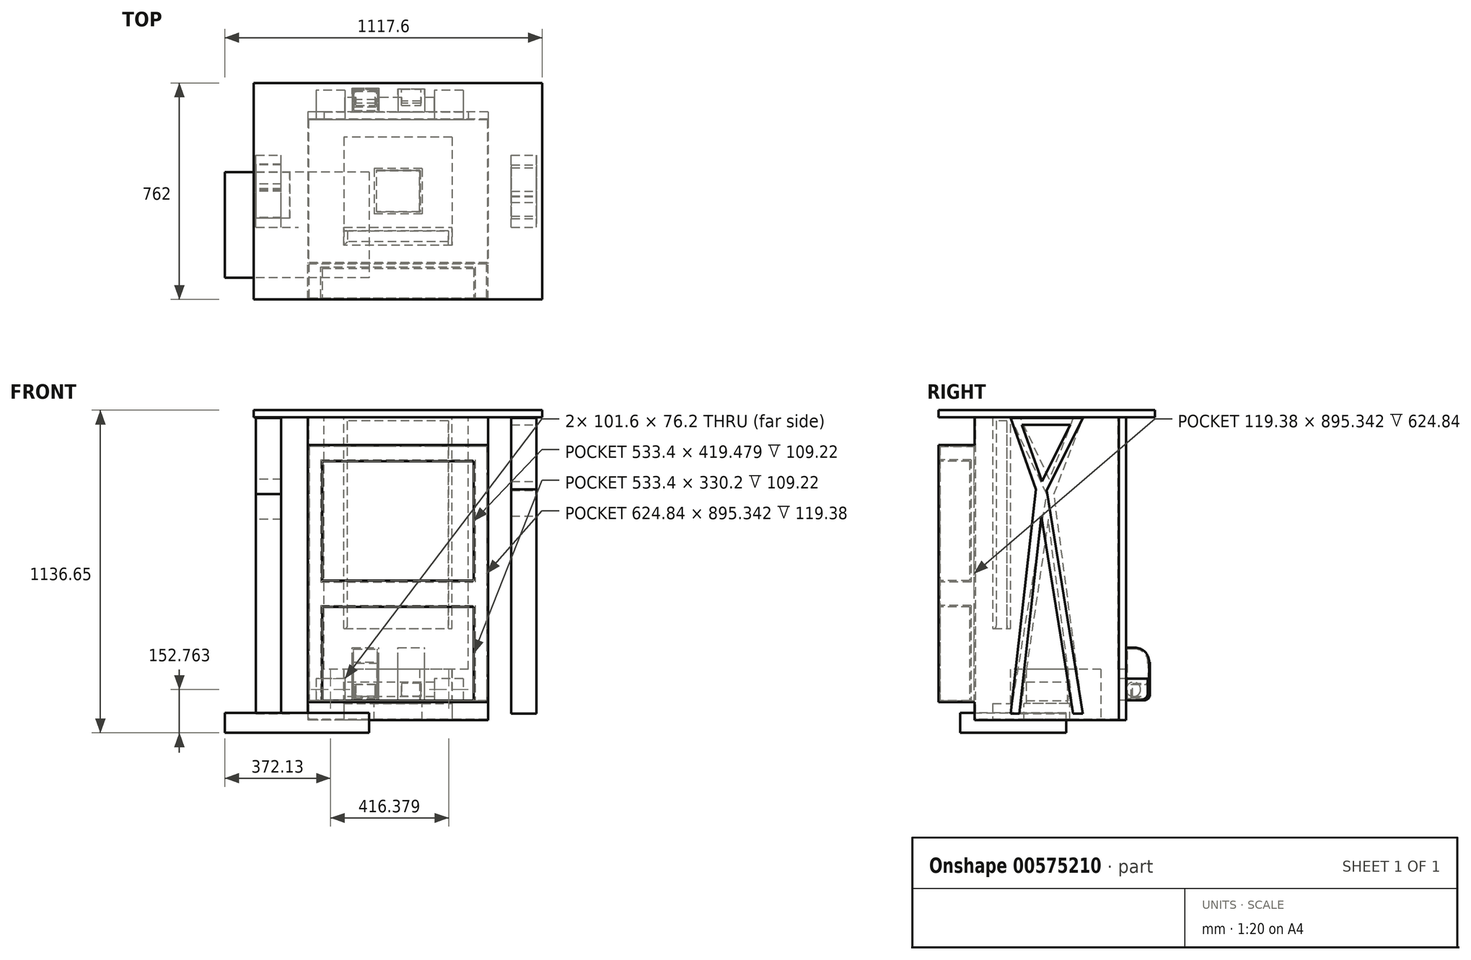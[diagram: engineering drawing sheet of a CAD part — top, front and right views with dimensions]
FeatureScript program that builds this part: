
annotation { "Feature Type Name" : "Feature", "Feature Type Description" : "" }
export const myFeature = defineFeature(function(context is Context, id is Id, definition is map)
    precondition{}
    {
        {
            var Q0;
            Q0=qCreatedBy(makeId("Top.planeOp"),FACE);
            var sketch = newSketch(context, id + "F0", { "sketchPlane" : qUnion([Q0])});
            skLineSegment(sketch, "E0.bottom", {"start": v(609.6, -304.8) * mm, "end": v(-609.6, -304.8) * mm});
            skLineSegment(sketch, "E0.top", {"start": v(609.6, 304.8) * mm, "end": v(-609.6, 304.8) * mm});
            skLineSegment(sketch, "E0.left", {"start": v(609.6, -304.8) * mm, "end": v(609.6, 304.8) * mm});
            skLineSegment(sketch, "E0.right", {"start": v(-609.6, -304.8) * mm, "end": v(-609.6, 304.8) * mm});
            skPoint(sketch, "E0.middle", {"position": v(0, 0) * mm});
            skLineSegment(sketch, "E1.bottom", {"start": v(102.15, -93.34) * mm, "end": v(-102.15, -93.34) * mm});
            skLineSegment(sketch, "E1.top", {"start": v(102.15, 93.34) * mm, "end": v(-102.15, 93.34) * mm});
            skLineSegment(sketch, "E1.left", {"start": v(102.15, -93.34) * mm, "end": v(102.15, 93.34) * mm});
            skLineSegment(sketch, "E1.right", {"start": v(-102.15, -93.34) * mm, "end": v(-102.15, 93.34) * mm});
            skLineSegment(sketch, "E2.bottom", {"start": v(102.15, -93.34) * mm, "end": v(609.6, -93.34) * mm});
            skLineSegment(sketch, "E2.top", {"start": v(102.15, 304.8) * mm, "end": v(609.6, 304.8) * mm});
            skLineSegment(sketch, "E2.left", {"start": v(102.15, -93.34) * mm, "end": v(102.15, 304.8) * mm});
            skLineSegment(sketch, "E2.right", {"start": v(609.6, -93.34) * mm, "end": v(609.6, 304.8) * mm});
            skLineSegment(sketch, "E3.bottom", {"start": v(69.43, 304.8) * mm, "end": v(-609.6, 304.8) * mm});
            skLineSegment(sketch, "E3.top", {"start": v(69.43, 93.34) * mm, "end": v(-609.6, 93.34) * mm});
            skLineSegment(sketch, "E3.left", {"start": v(69.43, 304.8) * mm, "end": v(69.43, 93.34) * mm});
            skLineSegment(sketch, "E3.right", {"start": v(-609.6, 304.8) * mm, "end": v(-609.6, 93.34) * mm});
            skLineSegment(sketch, "E4.bottom", {"start": v(-102.15, 67.6) * mm, "end": v(-609.6, 67.6) * mm});
            skLineSegment(sketch, "E4.top", {"start": v(-102.15, -304.8) * mm, "end": v(-609.6, -304.8) * mm});
            skLineSegment(sketch, "E4.left", {"start": v(-102.15, 67.6) * mm, "end": v(-102.15, -304.8) * mm});
            skLineSegment(sketch, "E4.right", {"start": v(-609.6, 67.6) * mm, "end": v(-609.6, -304.8) * mm});
            skLineSegment(sketch, "E5.bottom", {"start": v(-70.6, -93.34) * mm, "end": v(609.6, -93.34) * mm});
            skLineSegment(sketch, "E5.top", {"start": v(-70.6, -304.8) * mm, "end": v(609.6, -304.8) * mm});
            skLineSegment(sketch, "E5.left", {"start": v(-70.6, -93.34) * mm, "end": v(-70.6, -304.8) * mm});
            skLineSegment(sketch, "E5.right", {"start": v(609.6, -93.34) * mm, "end": v(609.6, -304.8) * mm});
            skLineSegment(sketch, "E6.top", {"start": v(102.15, -55.35) * mm, "end": v(609.6, -55.35) * mm});
            skLineSegment(sketch, "E6.left", {"start": v(102.15, 304.8) * mm, "end": v(102.15, -55.35) * mm});
            skLineSegment(sketch, "E6.right", {"start": v(609.6, 304.8) * mm, "end": v(609.6, -55.35) * mm});
            skSolve(sketch);
        }
        {
            var Q0;
            {var subQ3=sQuery(id+"F0.wireOp",EDGE,"E4.bottom");Q0=makeQuery(id+"F0.imprint","IMPRINT",FACE,{"disambiguationData":[TD([[makeQuery(id+"F0.imprint","IMPRINT",EDGE,{"derivedFrom":subQ3}),1.0]])]});}
            var sketch = newSketch(context, id + "F1", { "sketchPlane" : qUnion([Q0])});
            skSolve(sketch);
        }
        {
            var Q0;
            Q0=makeQuery(id+"F0.imprint","IMPRINT",FACE,{"disambiguationData":[TD([[makeQuery(id+"F0.imprint","IMPRINT",EDGE,{"derivedFrom":sQuery(id+"F0.wireOp",EDGE,"E3.bottom")}),1.0]])]});
            var Q1;
            {var subQ3=sQuery(id+"F0.wireOp",EDGE,"E2.top");Q1=makeQuery(id+"F0.imprint","IMPRINT",FACE,{"disambiguationData":[TD([[makeQuery(id+"F0.imprint","IMPRINT",EDGE,{"derivedFrom":subQ3}),-1.0]])]});}
            var Q2;
            Q2=makeQuery(id+"F0.imprint","IMPRINT",FACE,{"disambiguationData":[TD([[makeQuery(id+"F0.imprint","IMPRINT",EDGE,{"derivedFrom":sQuery(id+"F0.wireOp",EDGE,"E5.top")}),1.0]])]});
            var Q3;
            {var subQ3=sQuery(id+"F0.wireOp",EDGE,"E4.bottom");Q3=makeQuery(id+"F0.imprint","IMPRINT",FACE,{"disambiguationData":[TD([[makeQuery(id+"F0.imprint","IMPRINT",EDGE,{"derivedFrom":subQ3}),1.0]])]});}
            extrude(context, id + "F2", {"entities" : qUnion([Q0, Q1, Q2, Q3]), "oppositeDirection" : true, "depth" : 44.45 * mm, "offsetDistance" : 25.4 * mm});
        }
        {
            var Q0;
            {var subQ3=sQuery(id+"F0.wireOp",EDGE,"E4.bottom");Q0=makeQuery(id+"F1.imprint","IMPRINT",FACE,{"disambiguationData":[TD([[makeQuery(id+"F1.imprint","IMPRINT",EDGE,{"derivedFrom":makeQuery(id+"F0.imprint","IMPRINT",EDGE,{"derivedFrom":subQ3})}),1.0]])]});}
            extrude(context, id + "F3", {"entities" : qUnion([Q0]), "operationType" : NewBodyOperationType.ADD, "depth" : 25.4 * mm, "offsetDistance" : 25.4 * mm});
        }
        {
            var Q0;
            Q0=qCreatedBy(makeId("Top.planeOp"),FACE);
            var sketch = newSketch(context, id + "F4", { "sketchPlane" : qUnion([Q0])});
            skLineSegment(sketch, "E7.bottom", {"start": v(190.5, 190.5) * mm, "end": v(-190.5, 190.5) * mm});
            skLineSegment(sketch, "E7.top", {"start": v(190.5, -190.5) * mm, "end": v(-190.5, -190.5) * mm});
            skLineSegment(sketch, "E7.left", {"start": v(190.5, 190.5) * mm, "end": v(190.5, -190.5) * mm});
            skLineSegment(sketch, "E7.right", {"start": v(-190.5, 190.5) * mm, "end": v(-190.5, -190.5) * mm});
            skPoint(sketch, "E7.middle", {"position": v(0, 0) * mm});
            skSolve(sketch);
        }
        {
            var Q0;
            Q0=qCreatedBy(makeId("Top.planeOp"),FACE);
            var sketch = newSketch(context, id + "F5", { "sketchPlane" : qUnion([Q0])});
            skLineSegment(sketch, "E8.bottom", {"start": v(317.5, 254) * mm, "end": v(-317.5, 254) * mm});
            skLineSegment(sketch, "E8.top", {"start": v(317.5, -254) * mm, "end": v(-317.5, -254) * mm});
            skLineSegment(sketch, "E8.left", {"start": v(317.5, 254) * mm, "end": v(317.5, -254) * mm});
            skLineSegment(sketch, "E8.right", {"start": v(-317.5, 254) * mm, "end": v(-317.5, -254) * mm});
            skPoint(sketch, "E8.middle", {"position": v(0, 0) * mm});
            skSolve(sketch);
        }
        {
            var Q0;
            Q0 = qSketchRegion(id + "F5", true);
            var Q1;
            Q1=makeQuery(id+"F4.imprint","IMPRINT",FACE,{"disambiguationData":[TD([[makeQuery(id+"F4.imprint","IMPRINT",EDGE,{"derivedFrom":sQuery(id+"F4.wireOp",EDGE,"E7.bottom")}),1.0]])]});
            extrude(context, id + "F6", {"entities" : qUnion([Q0, Q1]), "depth" : 1066.8 * mm, "offsetDistance" : 25.4 * mm});
        }
        {
            var Q0;
            Q0=makeQuery(id+"F6.opExtrude","CAP_FACE",FACE,{"disambiguationData":[OSD([sQuery(id+"F5.wireOp",EDGE,"E8.bottom"),sQuery(id+"F5.wireOp",EDGE,"E8.top"),sQuery(id+"F5.wireOp",EDGE,"E8.left"),sQuery(id+"F5.wireOp",EDGE,"E8.right")])],"isStart":false});
            shell(context, id + "F7", {"entities" : qUnion([Q0]), "thickness" : 2.54 * mm});
        }
        {
            var Q0;
            Q0=makeQuery(id+"F6.opExtrude","SWEPT_FACE",FACE,{"disambiguationData":[OSD([sQuery(id+"F5.wireOp",EDGE,"E8.bottom")])]});
            var sketch = newSketch(context, id + "F8", { "sketchPlane" : qUnion([Q0])});
            skLineSegment(sketch, "E9.bottom", {"start": v(260.17, 1066.8) * mm, "end": v(-247.83, 1066.8) * mm});
            skLineSegment(sketch, "E9.top", {"start": v(260.17, 178.75) * mm, "end": v(-247.83, 178.75) * mm});
            skLineSegment(sketch, "E9.left", {"start": v(260.17, 1066.8) * mm, "end": v(260.17, 178.75) * mm});
            skLineSegment(sketch, "E9.right", {"start": v(-247.83, 1066.8) * mm, "end": v(-247.83, 178.75) * mm});
            skSolve(sketch);
        }
        {
            var Q0;
            Q0 = qSketchRegion(id + "F8", true);
            extrude(context, id + "F9", {"entities" : qUnion([Q0]), "operationType" : NewBodyOperationType.REMOVE, "oppositeDirection" : true, "depth" : 381 * mm, "offsetDistance" : 25.4 * mm});
        }
        {
            var Q0;
            Q0=makeQuery(id+"F6.opExtrude","SWEPT_FACE",FACE,{"disambiguationData":[OSD([sQuery(id+"F4.wireOp",EDGE,"E7.bottom")])]});
            var sketch = newSketch(context, id + "F10", { "sketchPlane" : qUnion([Q0])});
            skLineSegment(sketch, "E10.bottom", {"start": v(190.5, 185.28) * mm, "end": v(-190.5, 185.28) * mm});
            skLineSegment(sketch, "E10.top", {"start": v(190.5, 322.3) * mm, "end": v(-190.5, 322.3) * mm});
            skLineSegment(sketch, "E10.left", {"start": v(190.5, 185.28) * mm, "end": v(190.5, 322.3) * mm});
            skLineSegment(sketch, "E10.right", {"start": v(-190.5, 185.28) * mm, "end": v(-190.5, 322.3) * mm});
            skSolve(sketch);
        }
        {
            var Q0;
            Q0 = qSketchRegion(id + "F10", true);
            extrude(context, id + "F11", {"entities" : qUnion([Q0]), "operationType" : NewBodyOperationType.REMOVE, "oppositeDirection" : true, "depth" : 381 * mm, "offsetDistance" : 25.4 * mm});
        }
        {
            var Q0;
            Q0=makeQuery(id+"F11.boolean.opBoolean","COPY",FACE,{"derivedFrom":makeQuery(id+"F11.opExtrude","SWEPT_FACE",FACE,{"disambiguationData":[OSD([sQuery(id+"F10.wireOp",EDGE,"E10.bottom")])]})});
            extrude(context, id + "F12", {"entities" : qUnion([Q0]), "operationType" : NewBodyOperationType.REMOVE, "oppositeDirection" : true, "depth" : 127 * mm, "offsetDistance" : 25.4 * mm});
        }
        {
            var Q0;
            Q0=qCreatedBy(makeId("Top.planeOp"),FACE);
            cPlane(context, id + "F13", {"entities" : qUnion([Q0]), "cplaneType" : CPlaneType.OFFSET, "offset" : 1066.8 * mm, "width" : 152.4 * mm, "height" : 152.4 * mm});
        }
        {
            var Q0;
            Q0=qCreatedBy(id+"F13.planeOp",FACE);
            var sketch = newSketch(context, id + "F14", { "sketchPlane" : qUnion([Q0])});
            skLineSegment(sketch, "E11.bottom", {"start": v(508, 381) * mm, "end": v(-508, 381) * mm});
            skLineSegment(sketch, "E11.top", {"start": v(508, -381) * mm, "end": v(-508, -381) * mm});
            skLineSegment(sketch, "E11.left", {"start": v(508, 381) * mm, "end": v(508, -381) * mm});
            skLineSegment(sketch, "E11.right", {"start": v(-508, 381) * mm, "end": v(-508, -381) * mm});
            skPoint(sketch, "E11.middle", {"position": v(0, 0) * mm});
            skSolve(sketch);
        }
        {
            var Q0;
            Q0 = qSketchRegion(id + "F14", true);
            extrude(context, id + "F15", {"entities" : qUnion([Q0]), "depth" : 25.4 * mm, "offsetDistance" : 25.4 * mm});
        }
        {
            var Q0;
            Q0=qCreatedBy(makeId("Top.planeOp"),FACE);
            var sketch = newSketch(context, id + "F16", { "sketchPlane" : qUnion([Q0])});
            skLineSegment(sketch, "E12.bottom", {"start": v(-78.63, 74.3) * mm, "end": v(78.63, 74.3) * mm});
            skLineSegment(sketch, "E12.top", {"start": v(-78.63, -74.3) * mm, "end": v(78.63, -74.3) * mm});
            skLineSegment(sketch, "E12.left", {"start": v(-78.63, 74.3) * mm, "end": v(-78.63, -74.3) * mm});
            skLineSegment(sketch, "E12.right", {"start": v(78.63, 74.3) * mm, "end": v(78.63, -74.3) * mm});
            skPoint(sketch, "E12.middle", {"position": v(0, 0) * mm});
            skSolve(sketch);
        }
        {
            var Q0;
            Q0=makeQuery(id+"F15.opExtrude","CAP_FACE",FACE,{"disambiguationData":[OSD([sQuery(id+"F14.wireOp",EDGE,"E11.bottom"),sQuery(id+"F14.wireOp",EDGE,"E11.top"),sQuery(id+"F14.wireOp",EDGE,"E11.left"),sQuery(id+"F14.wireOp",EDGE,"E11.right")])],"isStart":true});
            cPlane(context, id + "F17", {"entities" : qUnion([Q0]), "cplaneType" : CPlaneType.OFFSET, "offset" : 2.54 * mm, "width" : 152.4 * mm, "height" : 152.4 * mm});
        }
        {
            var Q0;
            Q0=qCreatedBy(id+"F17.planeOp",FACE);
            cPlane(context, id + "F18", {"entities" : qUnion([Q0]), "cplaneType" : CPlaneType.OFFSET, "offset" : 995.68 * mm, "width" : 152.4 * mm, "height" : 152.4 * mm});
        }
        {
            var Q0;
            Q0=qCreatedBy(id+"F17.planeOp",FACE);
            var sketch = newSketch(context, id + "F19", { "sketchPlane" : qUnion([Q0])});
            skLineSegment(sketch, "E13.bottom", {"start": v(399.1, 127) * mm, "end": v(488, 127) * mm});
            skLineSegment(sketch, "E13.top", {"start": v(399.1, -127) * mm, "end": v(488, -127) * mm});
            skLineSegment(sketch, "E13.left", {"start": v(399.1, 127) * mm, "end": v(399.1, -127) * mm});
            skLineSegment(sketch, "E13.right", {"start": v(488, 127) * mm, "end": v(488, -127) * mm});
            skPoint(sketch, "E13.middle", {"position": v(443.56, 0) * mm});
            skLineSegment(sketch, "E14.bottom", {"start": v(-500.34, 127) * mm, "end": v(-411.44, 127) * mm});
            skLineSegment(sketch, "E14.top", {"start": v(-500.34, -127) * mm, "end": v(-411.44, -127) * mm});
            skLineSegment(sketch, "E14.left", {"start": v(-500.34, 127) * mm, "end": v(-500.34, -127) * mm});
            skLineSegment(sketch, "E14.right", {"start": v(-411.44, 127) * mm, "end": v(-411.44, -127) * mm});
            skPoint(sketch, "E14.middle", {"position": v(-455.89, 0) * mm});
            skSolve(sketch);
        }
        {
            var Q0;
            Q0 = qSketchRegion(id + "F19", true);
            extrude(context, id + "F20", {"entities" : qUnion([Q0]), "depth" : 1041.4 * mm, "offsetDistance" : 25.4 * mm});
        }
        {
            var Q0;
            Q0=makeQuery(id+"F6.opExtrude","SWEPT_FACE",FACE,{"disambiguationData":[OSD([sQuery(id+"F5.wireOp",EDGE,"E8.bottom")])]});
            var sketch = newSketch(context, id + "F21", { "sketchPlane" : qUnion([Q0])});
            skLineSegment(sketch, "E15.bottom", {"start": v(186.67, 146.41) * mm, "end": v(288.27, 146.41) * mm});
            skLineSegment(sketch, "E15.top", {"start": v(186.67, 70.21) * mm, "end": v(288.27, 70.21) * mm});
            skLineSegment(sketch, "E15.left", {"start": v(186.67, 146.41) * mm, "end": v(186.67, 70.21) * mm});
            skLineSegment(sketch, "E15.right", {"start": v(288.27, 146.41) * mm, "end": v(288.27, 70.21) * mm});
            skPoint(sketch, "E15.middle", {"position": v(237.47, 108.31) * mm});
            skLineSegment(sketch, "E16.bottom", {"start": v(-229.7, 146.41) * mm, "end": v(-128.1, 146.41) * mm});
            skLineSegment(sketch, "E16.top", {"start": v(-229.7, 70.21) * mm, "end": v(-128.1, 70.21) * mm});
            skLineSegment(sketch, "E16.left", {"start": v(-229.7, 146.41) * mm, "end": v(-229.7, 70.21) * mm});
            skLineSegment(sketch, "E16.right", {"start": v(-128.1, 146.41) * mm, "end": v(-128.1, 70.21) * mm});
            skPoint(sketch, "E16.middle", {"position": v(-178.9, 108.31) * mm});
            skSolve(sketch);
        }
        {
            var Q0;
            Q0 = qSketchRegion(id + "F21", true);
            extrude(context, id + "F22", {"entities" : qUnion([Q0]), "operationType" : NewBodyOperationType.ADD, "depth" : 101.6 * mm, "offsetDistance" : 25.4 * mm});
        }
        {
            var Q0;
            Q0=makeQuery(id+"F20.opExtrude","SWEPT_FACE",FACE,{"disambiguationData":[OSD([sQuery(id+"F19.wireOp",EDGE,"E14.left")])]});
            var sketch = newSketch(context, id + "F23", { "sketchPlane" : qUnion([Q0])});
            skLineSegment(sketch, "E17", {"start": v(127, 22.86) * mm, "end": v(0, 795.86) * mm});
            skLineSegment(sketch, "E18", {"start": v(0, 795.86) * mm, "end": v(127, 1064.26) * mm});
            skLineSegment(sketch, "E19", {"start": v(127, 1064.26) * mm, "end": v(127, 22.86) * mm});
            skLineSegment(sketch, "E20", {"start": v(-127, 22.86) * mm, "end": v(-25.27, 795.86) * mm});
            skLineSegment(sketch, "E21", {"start": v(-25.27, 795.86) * mm, "end": v(-127, 1064.26) * mm});
            skLineSegment(sketch, "E22", {"start": v(-127, 1064.26) * mm, "end": v(-127, 22.86) * mm});
            skSolve(sketch);
        }
        {
            var Q0;
            Q0 = qSketchRegion(id + "F23", true);
            extrude(context, id + "F24", {"entities" : qUnion([Q0]), "operationType" : NewBodyOperationType.REMOVE, "oppositeDirection" : true, "depth" : 149.86 * mm, "offsetDistance" : 25.4 * mm});
        }
        {
            var Q0;
            Q0=makeQuery(id+"F20.opExtrude","SWEPT_FACE",FACE,{"disambiguationData":[OSD([sQuery(id+"F19.wireOp",EDGE,"E13.right")])]});
            var sketch = newSketch(context, id + "F25", { "sketchPlane" : qUnion([Q0])});
            skLineSegment(sketch, "E23", {"start": v(127, 22.86) * mm, "end": v(0, 809.52) * mm});
            skLineSegment(sketch, "E24", {"start": v(0, 809.52) * mm, "end": v(127, 1064.26) * mm});
            skLineSegment(sketch, "E25", {"start": v(127, 1064.26) * mm, "end": v(127, 22.86) * mm});
            skLineSegment(sketch, "E26", {"start": v(-127, 22.86) * mm, "end": v(-38.8, 812.46) * mm});
            skLineSegment(sketch, "E27", {"start": v(-38.8, 812.46) * mm, "end": v(-127, 1064.26) * mm});
            skLineSegment(sketch, "E28", {"start": v(-127, 1064.26) * mm, "end": v(-127, 22.86) * mm});
            skSolve(sketch);
        }
        {
            var Q0;
            Q0 = qSketchRegion(id + "F25", true);
            extrude(context, id + "F26", {"entities" : qUnion([Q0]), "operationType" : NewBodyOperationType.REMOVE, "oppositeDirection" : true, "depth" : 152.4 * mm, "offsetDistance" : 25.4 * mm});
        }
        {
            var Q0;
            Q0=makeQuery(id+"F22.opExtrude","SWEPT_FACE",FACE,{"disambiguationData":[OSD([sQuery(id+"F21.wireOp",EDGE,"E15.left")])]});
            var sketch = newSketch(context, id + "F27", { "sketchPlane" : qUnion([Q0])});
            skCircle(sketch, "E29", {"center": v(304.8, 108.31) * mm, "radius": 25.4 * mm});
            skSolve(sketch);
        }
        {
            var Q0;
            Q0 = qSketchRegion(id + "F27", true);
            extrude(context, id + "F28", {"entities" : qUnion([Q0]), "operationType" : NewBodyOperationType.ADD, "depth" : 317.5 * mm, "offsetDistance" : 25.4 * mm});
        }
        {
            var Q0;
            Q0=qCreatedBy(id+"F18.planeOp",FACE);
            var sketch = newSketch(context, id + "F29", { "sketchPlane" : qUnion([Q0])});
            skLineSegment(sketch, "E30.bottom", {"start": v(-74.63, 72.67) * mm, "end": v(76.6, 72.67) * mm});
            skLineSegment(sketch, "E30.top", {"start": v(-74.63, -74.63) * mm, "end": v(76.6, -74.63) * mm});
            skLineSegment(sketch, "E30.left", {"start": v(-74.63, 72.67) * mm, "end": v(-74.63, -74.63) * mm});
            skLineSegment(sketch, "E30.right", {"start": v(76.6, 72.67) * mm, "end": v(76.6, -74.63) * mm});
            skSolve(sketch);
        }
        {
            var Q0;
            Q0 = qSketchRegion(id + "F29", true);
            extrude(context, id + "F30", {"entities" : qUnion([Q0]), "operationType" : NewBodyOperationType.REMOVE, "oppositeDirection" : true, "depth" : 281.94 * mm, "offsetDistance" : 25.4 * mm});
        }
        {
            var Q0;
            Q0=makeQuery(id+"F11.boolean.opBoolean","COPY",FACE,{"derivedFrom":makeQuery(id+"F11.opExtrude","SWEPT_FACE",FACE,{"disambiguationData":[OSD([sQuery(id+"F10.wireOp",EDGE,"E10.top")])]})});
            shell(context, id + "F31", {"entities" : qUnion([Q0]), "thickness" : 12.7 * mm});
        }
        {
            var Q0;
            Q0=makeQuery(id+"F20.opExtrude","SWEPT_FACE",FACE,{"disambiguationData":[OSD([sQuery(id+"F19.wireOp",EDGE,"E13.right")])]});
            var sketch = newSketch(context, id + "F32", { "sketchPlane" : qUnion([Q0])});
            skLineSegment(sketch, "E31", {"start": v(-16.64, 840.86) * mm, "end": v(82.5, 1039.74) * mm});
            skLineSegment(sketch, "E32", {"start": v(82.5, 1039.74) * mm, "end": v(-87.97, 1039.74) * mm});
            skLineSegment(sketch, "E33", {"start": v(-87.97, 1039.74) * mm, "end": v(-16.64, 840.86) * mm});
            skLineSegment(sketch, "E34", {"start": v(92.72, 22.86) * mm, "end": v(-18.93, 718.4) * mm});
            skLineSegment(sketch, "E35", {"start": v(-18.93, 718.4) * mm, "end": v(-96.62, 22.86) * mm});
            skLineSegment(sketch, "E36", {"start": v(-96.62, 22.86) * mm, "end": v(92.72, 22.86) * mm});
            skSolve(sketch);
        }
        {
            var Q0;
            Q0 = qSketchRegion(id + "F32", true);
            extrude(context, id + "F33", {"entities" : qUnion([Q0]), "operationType" : NewBodyOperationType.REMOVE, "oppositeDirection" : true, "depth" : 109.22 * mm, "offsetDistance" : 25.4 * mm});
        }
        {
            var Q0;
            Q0=makeQuery(id+"F20.opExtrude","SWEPT_FACE",FACE,{"disambiguationData":[OSD([sQuery(id+"F19.wireOp",EDGE,"E14.left")])]});
            var sketch = newSketch(context, id + "F34", { "sketchPlane" : qUnion([Q0])});
            skLineSegment(sketch, "E37", {"start": v(-9.1, 849) * mm, "end": v(92.76, 1064.26) * mm});
            skLineSegment(sketch, "E38", {"start": v(92.76, 1064.26) * mm, "end": v(-92.72, 1064.26) * mm});
            skLineSegment(sketch, "E39", {"start": v(-92.72, 1064.26) * mm, "end": v(-9.1, 849) * mm});
            skLineSegment(sketch, "E40", {"start": v(95.1, 22.86) * mm, "end": v(-95.1, 22.86) * mm});
            skLineSegment(sketch, "E41", {"start": v(-95.1, 22.86) * mm, "end": v(-5.06, 707.1) * mm});
            skLineSegment(sketch, "E42", {"start": v(-5.06, 707.1) * mm, "end": v(95.1, 22.86) * mm});
            skSolve(sketch);
        }
        {
            var Q0;
            Q0 = qSketchRegion(id + "F34", true);
            extrude(context, id + "F35", {"entities" : qUnion([Q0]), "operationType" : NewBodyOperationType.REMOVE, "oppositeDirection" : true, "depth" : 119.38 * mm, "offsetDistance" : 25.4 * mm});
        }
        {
            var Q0;
            Q0=makeQuery(id+"F11.boolean.opBoolean","COPY",EDGE,{"derivedFrom":makeQuery(id+"F11.opExtrude","CAP_EDGE",EDGE,{"disambiguationData":[OSD([sQuery(id+"F10.wireOp",EDGE,"E10.top")])],"isStart":true})});
            var Q1;
            Q1=makeQuery(id+"F31.opShell","OFFSET_EDGE",EDGE,{"disambiguationData":[OSD([sQuery(id+"F4.wireOp",EDGE,"E7.bottom"),sQuery(id+"F4.wireOp",EDGE,"E7.right"),sQuery(id+"F10.wireOp",EDGE,"E10.top"),sQuery(id+"F10.wireOp",EDGE,"E10.left")])]});
            var Q2;
            {var subQ0=sQuery(id+"F10.wireOp",EDGE,"E10.top");Q2=makeQuery(id+"F31.opShell","OFFSET_EDGE",EDGE,{"disambiguationData":[OSD([subQ0]),TDD([makeQuery(id+"F11.boolean.opBoolean","COPY",EDGE,{"derivedFrom":makeQuery(id+"F11.opExtrude","CAP_EDGE",EDGE,{"disambiguationData":[OSD([subQ0])],"isStart":true})})])]});}
            fillet(context, id + "F36", {"entities" : qUnion([Q0, Q1, Q2]), "radius" : 10.16 * mm, "tangentPropagation" : true, "allowEdgeOverflow" : false});
        }
        {
            var Q0;
            Q0=makeQuery(id+"F22.opExtrude","CAP_EDGE",EDGE,{"disambiguationData":[OSD([sQuery(id+"F21.wireOp",EDGE,"E15.top")])],"isStart":false});
            var Q1;
            Q1=makeQuery(id+"F22.opExtrude","CAP_EDGE",EDGE,{"disambiguationData":[OSD([sQuery(id+"F21.wireOp",EDGE,"E16.top")])],"isStart":false});
            fillet(context, id + "F37", {"entities" : qUnion([Q0, Q1]), "radius" : 25.4 * mm, "tangentPropagation" : true, "allowEdgeOverflow" : false});
        }
        {
            var Q0;
            Q0=makeQuery(id+"F6.opExtrude","SWEPT_FACE",FACE,{"disambiguationData":[OSD([sQuery(id+"F5.wireOp",EDGE,"E8.top")])]});
            var sketch = newSketch(context, id + "F38", { "sketchPlane" : qUnion([Q0])});
            skLineSegment(sketch, "E43.bottom", {"start": v(-317.5, 969.08) * mm, "end": v(317.5, 969.08) * mm});
            skLineSegment(sketch, "E43.top", {"start": v(-317.5, 63.58) * mm, "end": v(317.5, 63.58) * mm});
            skLineSegment(sketch, "E43.left", {"start": v(-317.5, 969.08) * mm, "end": v(-317.5, 63.58) * mm});
            skLineSegment(sketch, "E43.right", {"start": v(317.5, 969.08) * mm, "end": v(317.5, 63.58) * mm});
            skPoint(sketch, "E43.middle", {"position": v(0, 516.33) * mm});
            skSolve(sketch);
        }
        {
            var Q0;
            Q0 = qSketchRegion(id + "F38", true);
            extrude(context, id + "F39", {"entities" : qUnion([Q0]), "operationType" : NewBodyOperationType.ADD, "depth" : 127 * mm, "offsetDistance" : 25.4 * mm});
        }
        {
            var Q0;
            Q0=makeQuery(id+"F39.opExtrude","CAP_FACE",FACE,{"disambiguationData":[OSD([sQuery(id+"F38.wireOp",EDGE,"E43.bottom"),sQuery(id+"F38.wireOp",EDGE,"E43.top"),sQuery(id+"F38.wireOp",EDGE,"E43.left"),sQuery(id+"F38.wireOp",EDGE,"E43.right")])],"isStart":false});
            var sketch = newSketch(context, id + "F40", { "sketchPlane" : qUnion([Q0])});
            skLineSegment(sketch, "E44.bottom", {"start": v(-266.7, 399.3) * mm, "end": v(266.7, 399.3) * mm});
            skLineSegment(sketch, "E44.top", {"start": v(-266.7, 69.1) * mm, "end": v(266.7, 69.1) * mm});
            skLineSegment(sketch, "E44.left", {"start": v(-266.7, 399.3) * mm, "end": v(-266.7, 69.1) * mm});
            skLineSegment(sketch, "E44.right", {"start": v(266.7, 399.3) * mm, "end": v(266.7, 69.1) * mm});
            skPoint(sketch, "E44.middle", {"position": v(0, 234.2) * mm});
            skLineSegment(sketch, "E45.bottom", {"start": v(-266.7, 911.56) * mm, "end": v(266.7, 911.56) * mm});
            skLineSegment(sketch, "E45.top", {"start": v(-266.7, 492.08) * mm, "end": v(266.7, 492.08) * mm});
            skLineSegment(sketch, "E45.left", {"start": v(-266.7, 911.56) * mm, "end": v(-266.7, 492.08) * mm});
            skLineSegment(sketch, "E45.right", {"start": v(266.7, 911.56) * mm, "end": v(266.7, 492.08) * mm});
            skPoint(sketch, "E45.middle", {"position": v(0, 701.82) * mm});
            skSolve(sketch);
        }
        {
            var Q0;
            Q0 = qSketchRegion(id + "F40", true);
            extrude(context, id + "F41", {"entities" : qUnion([Q0]), "operationType" : NewBodyOperationType.REMOVE, "oppositeDirection" : true, "depth" : 109.22 * mm, "offsetDistance" : 25.4 * mm});
        }
        {
            var Q0;
            Q0=makeQuery(id+"F6.opExtrude","SWEPT_FACE",FACE,{"disambiguationData":[OSD([sQuery(id+"F5.wireOp",EDGE,"E8.bottom")])]});
            extrude(context, id + "F42", {"entities" : qUnion([Q0]), "depth" : 25.4 * mm, "offsetDistance" : 25.4 * mm});
        }
        {
            var Q0;
            Q0=makeQuery(id+"F42.opExtrude","CAP_FACE",FACE,{"disambiguationData":[OSD([sQuery(id+"F5.wireOp",EDGE,"E8.bottom")])],"isStart":false});
            var sketch = newSketch(context, id + "F43", { "sketchPlane" : qUnion([Q0])});
            skPoint(sketch, "E46.firstSnap0", {"position": v(237.47, 70.21) * mm});
            skLineSegment(sketch, "E46.bottom", {"start": v(161.22, 70.21) * mm, "end": v(67.24, 70.21) * mm});
            skLineSegment(sketch, "E46.top", {"start": v(161.22, 255.63) * mm, "end": v(67.24, 255.63) * mm});
            skLineSegment(sketch, "E46.left", {"start": v(161.22, 70.21) * mm, "end": v(161.22, 255.63) * mm});
            skLineSegment(sketch, "E46.right", {"start": v(67.24, 70.21) * mm, "end": v(67.24, 255.63) * mm});
            skLineSegment(sketch, "E47.bottom", {"start": v(0, 70.21) * mm, "end": v(-93.98, 70.21) * mm});
            skLineSegment(sketch, "E47.top", {"start": v(0, 255.63) * mm, "end": v(-93.98, 255.63) * mm});
            skLineSegment(sketch, "E47.left", {"start": v(0, 70.21) * mm, "end": v(0, 255.63) * mm});
            skLineSegment(sketch, "E47.right", {"start": v(-93.98, 70.21) * mm, "end": v(-93.98, 255.63) * mm});
            skSolve(sketch);
        }
        {
            var Q0;
            Q0 = qSketchRegion(id + "F43", true);
            extrude(context, id + "F44", {"entities" : qUnion([Q0]), "depth" : 81.28 * mm, "offsetDistance" : 25.4 * mm});
        }
        {
            var Q0;
            Q0=makeQuery(id+"F44.opExtrude","CAP_EDGE",EDGE,{"disambiguationData":[OSD([sQuery(id+"F43.wireOp",EDGE,"E47.top")])],"isStart":false});
            var Q1;
            Q1=makeQuery(id+"F44.opExtrude","CAP_EDGE",EDGE,{"disambiguationData":[OSD([sQuery(id+"F43.wireOp",EDGE,"E46.top")])],"isStart":false});
            fillet(context, id + "F45", {"entities" : qUnion([Q0, Q1]), "radius" : 50.8 * mm, "tangentPropagation" : true, "allowEdgeOverflow" : false});
        }
        {
            var Q0;
            Q0=makeQuery(id+"F44.opExtrude","CAP_FACE",FACE,{"disambiguationData":[OSD([sQuery(id+"F43.wireOp",EDGE,"E46.bottom"),sQuery(id+"F43.wireOp",EDGE,"E46.top"),sQuery(id+"F43.wireOp",EDGE,"E46.left"),sQuery(id+"F43.wireOp",EDGE,"E46.right")])],"isStart":false});
            extrude(context, id + "F46", {"entities" : qUnion([Q0]), "operationType" : NewBodyOperationType.ADD, "depth" : 2.54 * mm, "offsetDistance" : 25.4 * mm});
        }
        {
            var Q0;
            Q0=makeQuery(id+"F46.opExtrude","CAP_EDGE",EDGE,{"disambiguationData":[OSD([sQuery(id+"F43.wireOp",EDGE,"E46.bottom")])],"isStart":false});
            var Q1;
            Q1=makeQuery(id+"F44.opExtrude","CAP_EDGE",EDGE,{"disambiguationData":[OSD([sQuery(id+"F43.wireOp",EDGE,"E47.bottom")])],"isStart":false});
            fillet(context, id + "F47", {"entities" : qUnion([Q0, Q1]), "radius" : 20.32 * mm, "tangentPropagation" : true, "allowEdgeOverflow" : false});
        }
        {
            var Q0;
            Q0=makeQuery(id+"F46.opExtrude","CAP_FACE",FACE,{"disambiguationData":[OSD([sQuery(id+"F43.wireOp",EDGE,"E46.bottom"),sQuery(id+"F43.wireOp",EDGE,"E46.top"),sQuery(id+"F43.wireOp",EDGE,"E46.left"),sQuery(id+"F43.wireOp",EDGE,"E46.right")])],"isStart":false});
            var sketch = newSketch(context, id + "F48", { "sketchPlane" : qUnion([Q0])});
            skLineSegment(sketch, "E48.bottom", {"start": v(148.52, 83.4) * mm, "end": v(79.94, 83.4) * mm});
            skLineSegment(sketch, "E48.top", {"start": v(148.52, 125.75) * mm, "end": v(79.94, 125.75) * mm});
            skLineSegment(sketch, "E48.left", {"start": v(148.52, 83.4) * mm, "end": v(148.52, 125.75) * mm});
            skLineSegment(sketch, "E48.right", {"start": v(79.94, 83.4) * mm, "end": v(79.94, 125.75) * mm});
            skLineSegment(sketch, "E49.bottom", {"start": v(-12.7, 83.4) * mm, "end": v(-81.28, 83.4) * mm});
            skLineSegment(sketch, "E49.top", {"start": v(-12.7, 130.3) * mm, "end": v(-81.28, 130.3) * mm});
            skLineSegment(sketch, "E49.left", {"start": v(-12.7, 83.4) * mm, "end": v(-12.7, 130.3) * mm});
            skLineSegment(sketch, "E49.right", {"start": v(-81.28, 83.4) * mm, "end": v(-81.28, 130.3) * mm});
            skSolve(sketch);
        }
        {
            var Q0;
            Q0 = qSketchRegion(id + "F48", true);
            extrude(context, id + "F49", {"entities" : qUnion([Q0]), "operationType" : NewBodyOperationType.REMOVE, "oppositeDirection" : true, "depth" : 60.96 * mm, "offsetDistance" : 25.4 * mm});
        }
        {
            var Q0;
            Q0=makeQuery(id+"F44.opExtrude","CAP_FACE",FACE,{"disambiguationData":[OSD([sQuery(id+"F43.wireOp",EDGE,"E47.bottom"),sQuery(id+"F43.wireOp",EDGE,"E47.top"),sQuery(id+"F43.wireOp",EDGE,"E47.left"),sQuery(id+"F43.wireOp",EDGE,"E47.right")])],"isStart":false});
            var sketch = newSketch(context, id + "F50", { "sketchPlane" : qUnion([Q0])});
            skLineSegment(sketch, "E50.bottom", {"start": v(-12.7, 83.55) * mm, "end": v(-81.28, 83.55) * mm});
            skLineSegment(sketch, "E50.top", {"start": v(-12.7, 127.5) * mm, "end": v(-81.28, 127.5) * mm});
            skLineSegment(sketch, "E50.left", {"start": v(-12.7, 83.55) * mm, "end": v(-12.7, 127.5) * mm});
            skLineSegment(sketch, "E50.right", {"start": v(-81.28, 83.55) * mm, "end": v(-81.28, 127.5) * mm});
            skSolve(sketch);
        }
        {
            var Q0;
            Q0 = qSketchRegion(id + "F50", true);
            extrude(context, id + "F51", {"entities" : qUnion([Q0]), "operationType" : NewBodyOperationType.REMOVE, "oppositeDirection" : true, "depth" : 25.4 * mm, "offsetDistance" : 25.4 * mm});
        }
        {
            var Q0;
            Q0=makeQuery(id+"F51.boolean.opBoolean","COPY",FACE,{"derivedFrom":makeQuery(id+"F51.opExtrude","SWEPT_FACE",FACE,{"disambiguationData":[OSD([sQuery(id+"F50.wireOp",EDGE,"E50.top")])]})});
            var Q1;
            Q1=makeQuery(id+"F49.boolean.opBoolean","COPY",FACE,{"derivedFrom":makeQuery(id+"F49.opExtrude","SWEPT_FACE",FACE,{"disambiguationData":[OSD([sQuery(id+"F48.wireOp",EDGE,"E48.top")])]})});
            shell(context, id + "F52", {"entities" : qUnion([Q0, Q1]), "thickness" : 5.08 * mm});
        }
        {
            var Q0;
            Q0=makeQuery(id+"F16.imprint","IMPRINT",FACE,{"disambiguationData":[TD([[makeQuery(id+"F16.imprint","IMPRINT",EDGE,{"derivedFrom":sQuery(id+"F16.wireOp",EDGE,"E12.bottom")}),-1.0]])]});
            var sketch = newSketch(context, id + "F53", { "sketchPlane" : qUnion([Q0])});
            skLineSegment(sketch, "E51.bottom", {"start": v(-74.62, -72.2) * mm, "end": v(78.26, -72.2) * mm});
            skLineSegment(sketch, "E51.top", {"start": v(-74.62, 72.2) * mm, "end": v(78.26, 72.2) * mm});
            skLineSegment(sketch, "E51.left", {"start": v(-74.62, -72.2) * mm, "end": v(-74.62, 72.2) * mm});
            skLineSegment(sketch, "E51.right", {"start": v(78.26, -72.2) * mm, "end": v(78.26, 72.2) * mm});
            skSolve(sketch);
        }
        {
            var Q0;
            Q0=makeQuery(id+"F12.boolean.opBoolean","COPY",FACE,{"derivedFrom":makeQuery(id+"F12.opExtrude","CAP_FACE",FACE,{"disambiguationData":[OSD([sQuery(id+"F10.wireOp",EDGE,"E10.bottom")])],"isStart":false})});
            var sketch = newSketch(context, id + "F54", { "sketchPlane" : qUnion([Q0])});
            skLineSegment(sketch, "E52.bottom", {"start": v(84.45, 80.53) * mm, "end": v(-84.45, 80.53) * mm});
            skLineSegment(sketch, "E52.top", {"start": v(84.45, -80.53) * mm, "end": v(-84.45, -80.53) * mm});
            skLineSegment(sketch, "E52.left", {"start": v(84.45, 80.53) * mm, "end": v(84.45, -80.53) * mm});
            skLineSegment(sketch, "E52.right", {"start": v(-84.45, 80.53) * mm, "end": v(-84.45, -80.53) * mm});
            skPoint(sketch, "E52.middle", {"position": v(0, 0) * mm});
            skSolve(sketch);
        }
        {
            var Q0;
            Q0 = qSketchRegion(id + "F54", true);
            var Q1;
            Q1=makeQuery(id+"F16.imprint","IMPRINT",FACE,{"disambiguationData":[TD([[makeQuery(id+"F16.imprint","IMPRINT",EDGE,{"derivedFrom":sQuery(id+"F16.wireOp",EDGE,"E12.bottom")}),-1.0]])]});
            extrude(context, id + "F55", {"entities" : qUnion([Q0, Q1]), "operationType" : NewBodyOperationType.REMOVE, "oppositeDirection" : true, "depth" : 441.96 * mm, "offsetDistance" : 25.4 * mm});
        }
        {
            var Q0;
            Q0=makeQuery(id+"F53.imprint","IMPRINT",FACE,{"disambiguationData":[TD([[makeQuery(id+"F53.imprint","IMPRINT",EDGE,{"derivedFrom":sQuery(id+"F53.wireOp",EDGE,"E51.bottom")}),1.0]])]});
            extrude(context, id + "F56", {"entities" : qUnion([Q0]), "operationType" : NewBodyOperationType.REMOVE, "depth" : 134.62 * mm, "offsetDistance" : 25.4 * mm});
        }
    });
